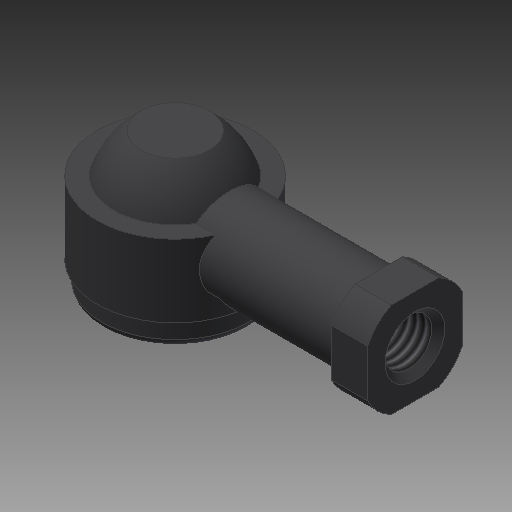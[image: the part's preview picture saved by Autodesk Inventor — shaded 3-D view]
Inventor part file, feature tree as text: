
AUTODESK INVENTOR PART (.ipt)
format: ipt  version: 2018 (Build 220112000, 112)  size: 244,224 bytes
history: native  units: mm
features: sketch x9, other x7, revolve x6, extrude x2, hole x1
ambient origin geometry x8: Origin, YZ Plane, XZ Plane, XY Plane, X Axis, Y Axis, Z Axis, Center Point
bodies: Solid1 (feature_tree)
feature tree (25):
  revolve  "Revolution1"  [1 undecoded]
  extrude  "Extrusion1"  TaperAngle=360.0deg  [1 undecoded]
  revolve  "Revolution2"  Angle=360.0deg
  revolve  "Revolution3"  [1 undecoded]
  revolve  "Revolution4"  [1 undecoded]
  revolve  "Revolution5"  [1 undecoded]
  revolve  "Revolution6"  [1 undecoded]
  hole  "Hole1"  [1 undecoded]
  extrude  "Extrusion2"  [1 undecoded]
  other  "IP1_XY"
  other  "IP1_YZ"
  other  "IP1_ZX"
  other  "IP1_X"
  other  "IP1_Y"
  other  "IP1_Z"
  other  "IP1_Center"
  sketch  "Sketch_2"  dims[d0=360.0deg d1=38.0mm d2=0.0mm]
  sketch  "Sketch_16"
  sketch  "Sketch_12"  dims[d5=360.0deg d6=360.0deg]
  sketch  "Sketch_13"  dims[d7=360.0deg]
  sketch  "Sketch_14"  dims[d8=8.376mm d9=23.812mm d10=10.729mm d11=2.0mm d12=90.0deg d13=26.1765mm d14=120.0deg d15=6.5mm d16=0.0mm]
  sketch  "Sketch_15"
  sketch  "Sketch_17"
  sketch  "Sketch8"  dims[d3=360.0deg d4=360.0deg]
  sketch  "Sketch_20"
note: 8 required parameter values undecoded (feature->parameter linkage not recoverable at this tier; creation-order binding heuristic only, values carry confidence <= 0.55)